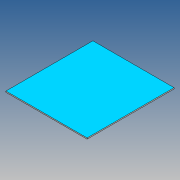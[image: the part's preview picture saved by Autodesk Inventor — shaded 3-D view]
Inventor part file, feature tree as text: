
AUTODESK INVENTOR PART (.ipt)
format: ipt  version: 2017 (Build 210142000, 142)  size: 83,968 bytes
history: native  units: mm
features: other x1, extrude x1, sketch x1
ambient origin geometry x8: Origin, YZ Plane, XZ Plane, XY Plane, X Axis, Y Axis, Z Axis, Center Point
bodies: Body1 (feature_tree)
feature tree (3):
  other  "Sólido1"
  extrude  "Extrusión1"  Depth=75.0mm
  sketch  "Boceto1"  dims[d0=70.0mm d1=75.0mm d2=1.0mm d3=0.0mm]
